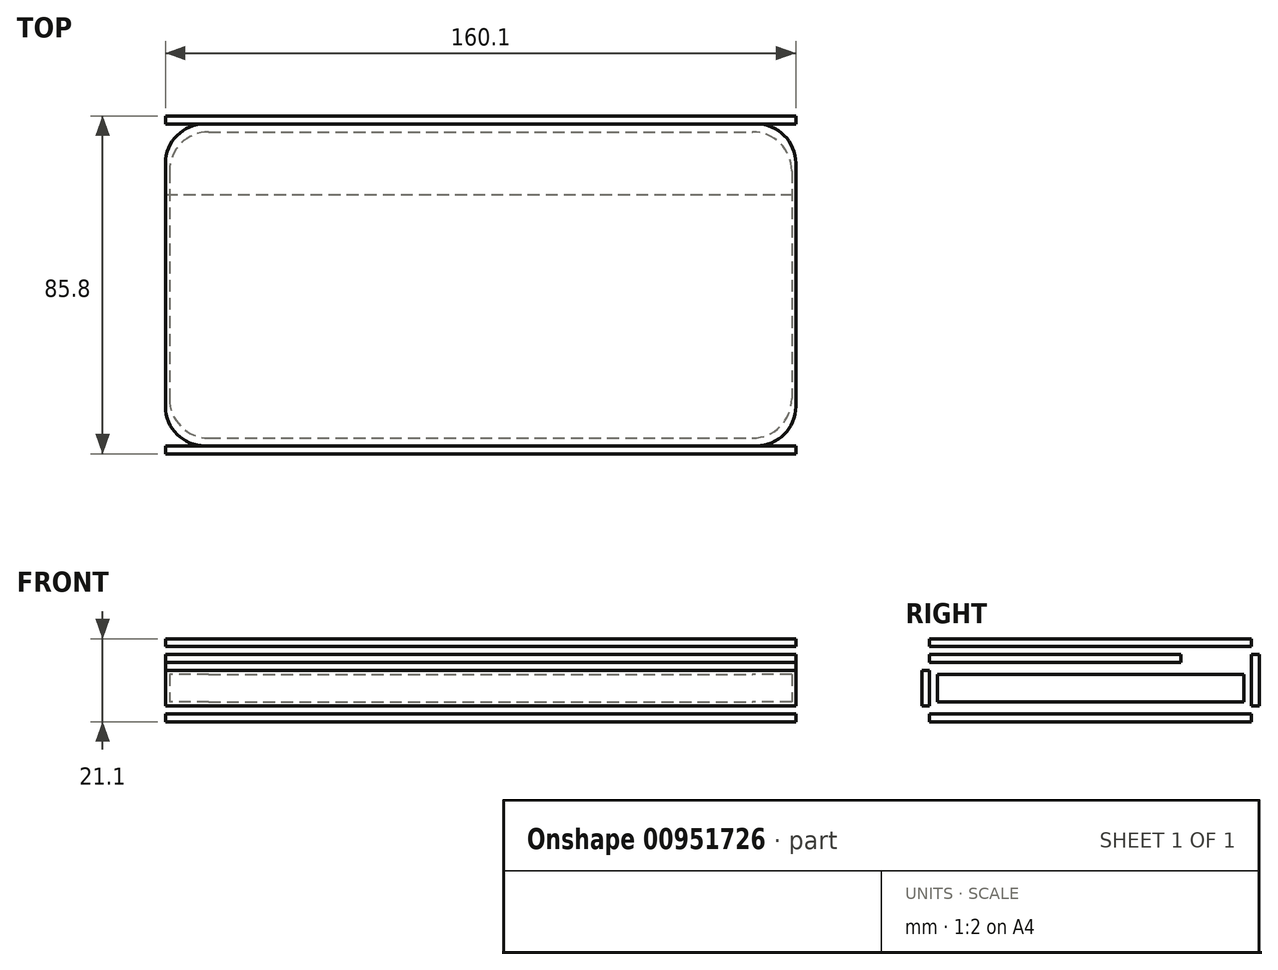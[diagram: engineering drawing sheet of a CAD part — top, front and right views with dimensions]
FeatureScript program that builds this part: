
annotation { "Feature Type Name" : "Feature", "Feature Type Description" : "" }
export const myFeature = defineFeature(function(context is Context, id is Id, definition is map)
    precondition{}
    {
        {
            var Q0;
            Q0=qCreatedBy(makeId("Top.planeOp"),FACE);
            var sketch = newSketch(context, id + "F0", { "sketchPlane" : qUnion([Q0])});
            skLineSegment(sketch, "E0.bottom", {"start": v(-69.05, 38.9) * mm, "end": v(69.05, 38.9) * mm});
            skLineSegment(sketch, "E0.top", {"start": v(-69.05, -38.9) * mm, "end": v(69.05, -38.9) * mm});
            skLineSegment(sketch, "E0.left", {"start": v(-79.05, 28.9) * mm, "end": v(-79.05, -28.9) * mm});
            skLineSegment(sketch, "E0.right", {"start": v(79.05, 28.9) * mm, "end": v(79.05, -28.9) * mm});
            skLineSegment(sketch, "E1", {"start": v(0, 38.9) * mm, "end": v(0, -38.9) * mm, "construction": true});
            skPoint(sketch, "E2.visualSharp", {"position": v(79.05, 38.9) * mm});
            skArc(sketch, "E2.filletArc", {"start": v(79.05, 28.9) * mm, "mid": v(76.12, 35.97) * mm, "end": v(69.05, 38.9) * mm});
            skPoint(sketch, "E3.visualSharp", {"position": v(79.05, -38.9) * mm});
            skArc(sketch, "E3.filletArc", {"start": v(69.05, -38.9) * mm, "mid": v(76.12, -35.97) * mm, "end": v(79.05, -28.9) * mm});
            skPoint(sketch, "E4.visualSharp", {"position": v(-79.05, 38.9) * mm});
            skArc(sketch, "E4.filletArc", {"start": v(-69.05, 38.9) * mm, "mid": v(-76.12, 35.97) * mm, "end": v(-79.05, 28.9) * mm});
            skPoint(sketch, "E5.visualSharp", {"position": v(-79.05, -38.9) * mm});
            skArc(sketch, "E5.filletArc", {"start": v(-79.05, -28.9) * mm, "mid": v(-76.12, -35.97) * mm, "end": v(-69.05, -38.9) * mm});
            skSolve(sketch);
        }
        {
            var Q0;
            Q0 = qSketchRegion(id + "F0", true);
            extrude(context, id + "F1", {"entities" : qUnion([Q0]), "depth" : 7.1 * mm, "offsetDistance" : 25 * mm});
        }
        {
            var Q0;
            Q0=makeQuery(id+"F1.opExtrude","SWEPT_FACE",FACE,{"disambiguationData":[OSD([sQuery(id+"F0.wireOp",EDGE,"E0.top")])]});
            cPlane(context, id + "F2", {"entities" : qUnion([Q0]), "cplaneType" : CPlaneType.OFFSET, "offset" : 2 * mm, "width" : 150 * mm, "height" : 150 * mm});
        }
        {
            var Q0;
            Q0=qCreatedBy(id+"F2.planeOp",FACE);
            var sketch = newSketch(context, id + "F3", { "sketchPlane" : qUnion([Q0])});
            skLineSegment(sketch, "E6", {"start": v(0, 0) * mm, "end": v(0, -1) * mm, "construction": true});
            skLineSegment(sketch, "E7", {"start": v(80.05, -1) * mm, "end": v(-80.05, -1) * mm});
            skLineSegment(sketch, "E8.0", {"start": v(69.05, 0) * mm, "end": v(79.05, 0) * mm, "construction": true});
            skLineSegment(sketch, "E9", {"start": v(79.05, 0) * mm, "end": v(80.05, 0) * mm, "construction": true});
            skLineSegment(sketch, "E10", {"start": v(80.05, -1) * mm, "end": v(80.05, 8.1) * mm});
            skLineSegment(sketch, "E11.0", {"start": v(69.05, 7.1) * mm, "end": v(69.05, 0) * mm, "construction": true});
            skLineSegment(sketch, "E12", {"start": v(69.05, 7.1) * mm, "end": v(69.05, 8.1) * mm, "construction": true});
            skLineSegment(sketch, "E13", {"start": v(80.05, 8.1) * mm, "end": v(-80.05, 8.1) * mm});
            skLineSegment(sketch, "E14", {"start": v(-80.05, 8.1) * mm, "end": v(-80.05, -1) * mm});
            skSolve(sketch);
        }
        {
            var Q0;
            Q0 = qSketchRegion(id + "F3", true);
            extrude(context, id + "F4", {"entities" : qUnion([Q0]), "depth" : 2 * mm, "offsetDistance" : 25 * mm});
        }
        {
            var Q0;
            Q0=makeQuery(id+"F4.opExtrude","SWEPT_BODY",BODY,{"disambiguationData":[OSD([sQuery(id+"F3.wireOp",EDGE,"E7"),sQuery(id+"F3.wireOp",EDGE,"E10"),sQuery(id+"F3.wireOp",EDGE,"E13"),sQuery(id+"F3.wireOp",EDGE,"E14")])]});
            var Q1;
            Q1=qCreatedBy(makeId("Front.planeOp"),FACE);
            mirror(context, id + "F5", {"entities" : qUnion([Q0]), "mirrorPlane" : qUnion([Q1])});
        }
        {
            var Q0;
            Q0=makeQuery(id+"F1.opExtrude","CAP_FACE",FACE,{"disambiguationData":[OSD([sQuery(id+"F0.wireOp",EDGE,"E0.bottom"),sQuery(id+"F0.wireOp",EDGE,"E0.top"),sQuery(id+"F0.wireOp",EDGE,"E0.left"),sQuery(id+"F0.wireOp",EDGE,"E0.right"),sQuery(id+"F0.wireOp",EDGE,"E2.filletArc"),sQuery(id+"F0.wireOp",EDGE,"E3.filletArc"),sQuery(id+"F0.wireOp",EDGE,"E4.filletArc"),sQuery(id+"F0.wireOp",EDGE,"E5.filletArc")])],"isStart":true});
            cPlane(context, id + "F6", {"entities" : qUnion([Q0]), "cplaneType" : CPlaneType.OFFSET, "offset" : 3 * mm, "width" : 150 * mm, "height" : 150 * mm});
        }
        {
            var Q0;
            Q0=qCreatedBy(id+"F6.planeOp",FACE);
            var sketch = newSketch(context, id + "F7", { "sketchPlane" : qUnion([Q0])});
            skLineSegment(sketch, "E15.0", {"start": v(70.05, 40.9) * mm, "end": v(-70.05, 40.9) * mm});
            skLineSegment(sketch, "E16.0", {"start": v(70.05, -40.9) * mm, "end": v(-70.05, -40.9) * mm});
            skLineSegment(sketch, "E17", {"start": v(-80.05, 30.9) * mm, "end": v(-80.05, -30.9) * mm});
            skLineSegment(sketch, "E18", {"start": v(80.05, 30.9) * mm, "end": v(80.05, -30.9) * mm});
            skPoint(sketch, "E19.visualSharp", {"position": v(-80.05, 40.9) * mm});
            skArc(sketch, "E19.filletArc", {"start": v(-70.05, 40.9) * mm, "mid": v(-77.12, 37.97) * mm, "end": v(-80.05, 30.9) * mm});
            skPoint(sketch, "E20.visualSharp", {"position": v(80.05, 40.9) * mm});
            skArc(sketch, "E20.filletArc", {"start": v(80.05, 30.9) * mm, "mid": v(77.12, 37.97) * mm, "end": v(70.05, 40.9) * mm});
            skPoint(sketch, "E21.visualSharp", {"position": v(80.05, -40.9) * mm});
            skArc(sketch, "E21.filletArc", {"start": v(70.05, -40.9) * mm, "mid": v(77.12, -37.97) * mm, "end": v(80.05, -30.9) * mm});
            skPoint(sketch, "E22.visualSharp", {"position": v(-80.05, -40.9) * mm});
            skArc(sketch, "E22.filletArc", {"start": v(-80.05, -30.9) * mm, "mid": v(-77.12, -37.97) * mm, "end": v(-70.05, -40.9) * mm});
            skSolve(sketch);
        }
        {
            var Q0;
            Q0 = qSketchRegion(id + "F7", true);
            extrude(context, id + "F8", {"entities" : qUnion([Q0]), "depth" : 2 * mm, "offsetDistance" : 25 * mm});
        }
        {
            var Q0;
            Q0=makeQuery(id+"F1.opExtrude","CAP_FACE",FACE,{"disambiguationData":[OSD([sQuery(id+"F0.wireOp",EDGE,"E0.bottom"),sQuery(id+"F0.wireOp",EDGE,"E0.top"),sQuery(id+"F0.wireOp",EDGE,"E0.left"),sQuery(id+"F0.wireOp",EDGE,"E0.right"),sQuery(id+"F0.wireOp",EDGE,"E2.filletArc"),sQuery(id+"F0.wireOp",EDGE,"E3.filletArc"),sQuery(id+"F0.wireOp",EDGE,"E4.filletArc"),sQuery(id+"F0.wireOp",EDGE,"E5.filletArc")])],"isStart":false});
            cPlane(context, id + "F9", {"entities" : qUnion([Q0]), "cplaneType" : CPlaneType.OFFSET, "offset" : 3 * mm, "width" : 150 * mm, "height" : 150 * mm});
        }
        {
            var Q0;
            Q0=qCreatedBy(id+"F9.planeOp",FACE);
            var sketch = newSketch(context, id + "F10", { "sketchPlane" : qUnion([Q0])});
            skLineSegment(sketch, "E23.0", {"start": v(70.05, -40.9) * mm, "end": v(-70.05, -40.9) * mm});
            skLineSegment(sketch, "E24.0", {"start": v(80.05, 40.9) * mm, "end": v(-80.05, 40.9) * mm, "construction": true});
            skLineSegment(sketch, "E25", {"start": v(-80.05, 40.9) * mm, "end": v(-80.05, 22.9) * mm, "construction": true});
            skLineSegment(sketch, "E26", {"start": v(-80.05, 22.9) * mm, "end": v(-80.05, -30.9) * mm});
            skLineSegment(sketch, "E27", {"start": v(-80.05, 22.9) * mm, "end": v(80.05, 22.9) * mm});
            skLineSegment(sketch, "E28", {"start": v(80.05, 22.9) * mm, "end": v(80.05, -30.9) * mm});
            skPoint(sketch, "E29.visualSharp", {"position": v(80.05, -40.9) * mm});
            skArc(sketch, "E29.filletArc", {"start": v(70.05, -40.9) * mm, "mid": v(77.12, -37.97) * mm, "end": v(80.05, -30.9) * mm});
            skPoint(sketch, "E30.visualSharp", {"position": v(-80.05, -40.9) * mm});
            skArc(sketch, "E30.filletArc", {"start": v(-80.05, -30.9) * mm, "mid": v(-77.12, -37.97) * mm, "end": v(-70.05, -40.9) * mm});
            skSolve(sketch);
        }
        {
            var Q0;
            Q0=makeQuery(id+"F10.imprint","IMPRINT",FACE,{"disambiguationData":[TD([[makeQuery(id+"F10.imprint","IMPRINT",EDGE,{"derivedFrom":sQuery(id+"F10.wireOp",EDGE,"E23.0")}),-1.0]])]});
            extrude(context, id + "F11", {"entities" : qUnion([Q0]), "depth" : 2 * mm, "offsetDistance" : 25 * mm});
        }
        {
            var Q0;
            Q0=makeQuery(id+"F11.opExtrude","CAP_FACE",FACE,{"disambiguationData":[OSD([sQuery(id+"F10.wireOp",EDGE,"E23.0"),sQuery(id+"F10.wireOp",EDGE,"E26"),sQuery(id+"F10.wireOp",EDGE,"E27"),sQuery(id+"F10.wireOp",EDGE,"E28"),sQuery(id+"F10.wireOp",EDGE,"E29.filletArc"),sQuery(id+"F10.wireOp",EDGE,"E30.filletArc")])],"isStart":false});
            cPlane(context, id + "F12", {"entities" : qUnion([Q0]), "cplaneType" : CPlaneType.OFFSET, "offset" : 2 * mm, "width" : 150 * mm, "height" : 150 * mm});
        }
        {
            var Q0;
            Q0=qCreatedBy(id+"F12.planeOp",FACE);
            var sketch = newSketch(context, id + "F13", { "sketchPlane" : qUnion([Q0])});
            skLineSegment(sketch, "E31.0", {"start": v(70.05, 40.9) * mm, "end": v(-70.05, 40.9) * mm});
            skLineSegment(sketch, "E31.1", {"start": v(70.05, -40.9) * mm, "end": v(-70.05, -40.9) * mm});
            skLineSegment(sketch, "E31.2", {"start": v(70.05, 40.9) * mm, "end": v(-70.05, 40.9) * mm});
            skLineSegment(sketch, "E32", {"start": v(-80.05, 30.9) * mm, "end": v(-80.05, -30.9) * mm});
            skLineSegment(sketch, "E33", {"start": v(80.05, 30.9) * mm, "end": v(80.05, -30.9) * mm});
            skPoint(sketch, "E34.visualSharp", {"position": v(-80.05, 40.9) * mm});
            skArc(sketch, "E34.filletArc", {"start": v(-70.05, 40.9) * mm, "mid": v(-77.12, 37.97) * mm, "end": v(-80.05, 30.9) * mm});
            skPoint(sketch, "E35.visualSharp", {"position": v(80.05, 40.9) * mm});
            skArc(sketch, "E35.filletArc", {"start": v(80.05, 30.9) * mm, "mid": v(77.12, 37.97) * mm, "end": v(70.05, 40.9) * mm});
            skPoint(sketch, "E36.visualSharp", {"position": v(80.05, -40.9) * mm});
            skArc(sketch, "E36.filletArc", {"start": v(70.05, -40.9) * mm, "mid": v(77.12, -37.97) * mm, "end": v(80.05, -30.9) * mm});
            skPoint(sketch, "E37.visualSharp", {"position": v(-80.05, -40.9) * mm});
            skArc(sketch, "E37.filletArc", {"start": v(-80.05, -30.9) * mm, "mid": v(-77.12, -37.97) * mm, "end": v(-70.05, -40.9) * mm});
            skSolve(sketch);
        }
        {
            var Q0;
            Q0 = qSketchRegion(id + "F13", true);
            extrude(context, id + "F14", {"entities" : qUnion([Q0]), "depth" : 2 * mm, "offsetDistance" : 25 * mm});
        }
        {
            var Q0;
            Q0=makeQuery(id+"F5.opPattern","COPY",FACE,{"derivedFrom":makeQuery(id+"F4.opExtrude","SWEPT_FACE",FACE,{"disambiguationData":[OSD([sQuery(id+"F3.wireOp",EDGE,"E13")])]}),"instanceName":"1"});
            extrude(context, id + "F15", {"entities" : qUnion([Q0]), "operationType" : NewBodyOperationType.ADD, "depth" : 4 * mm, "offsetDistance" : 25 * mm});
        }
    });
